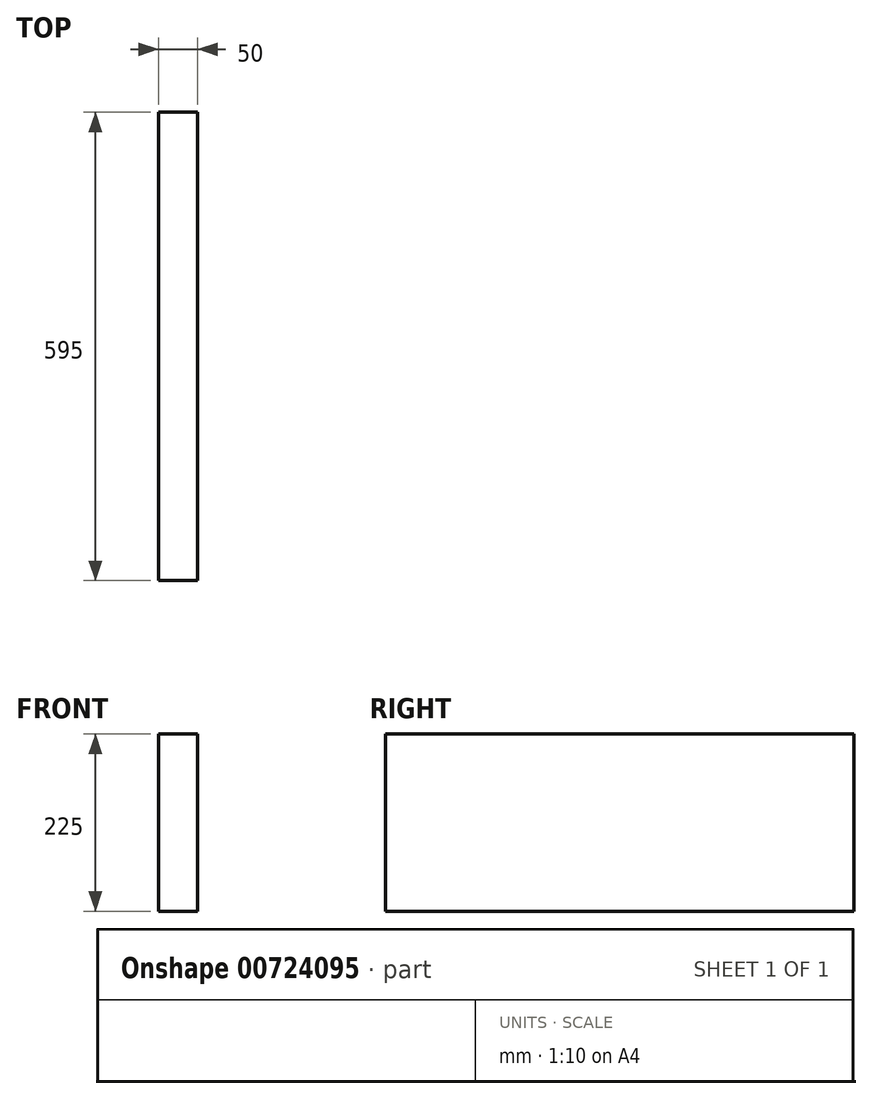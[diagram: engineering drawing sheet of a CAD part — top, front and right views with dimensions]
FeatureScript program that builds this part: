
annotation { "Feature Type Name" : "Feature", "Feature Type Description" : "" }
export const myFeature = defineFeature(function(context is Context, id is Id, definition is map)
    precondition{}
    {
        {
            var Q0;
            Q0=qCreatedBy(makeId("Right.planeOp"),FACE);
            var sketch = newSketch(context, id + "F0", { "sketchPlane" : qUnion([Q0])});
            skLineSegment(sketch, "E0.bottom", {"start": v(-297.5, 112.5) * mm, "end": v(297.5, 112.5) * mm});
            skLineSegment(sketch, "E0.top", {"start": v(-297.5, -112.5) * mm, "end": v(297.5, -112.5) * mm});
            skLineSegment(sketch, "E0.left", {"start": v(-297.5, 112.5) * mm, "end": v(-297.5, -112.5) * mm});
            skLineSegment(sketch, "E0.right", {"start": v(297.5, 112.5) * mm, "end": v(297.5, -112.5) * mm});
            skLineSegment(sketch, "E1", {"start": v(-297.5, 112.5) * mm, "end": v(297.5, -112.5) * mm, "construction": true});
            skLineSegment(sketch, "E2", {"start": v(297.5, 112.5) * mm, "end": v(-297.5, -112.5) * mm, "construction": true});
            skSolve(sketch);
        }
        {
            var Q0;
            Q0=qSketchRegion(id+"F0",true);
            extrude(context, id + "F1", {"entities" : qUnion([Q0]), "depth" : 50 * mm, "offsetDistance" : 25 * mm});
        }
    });
